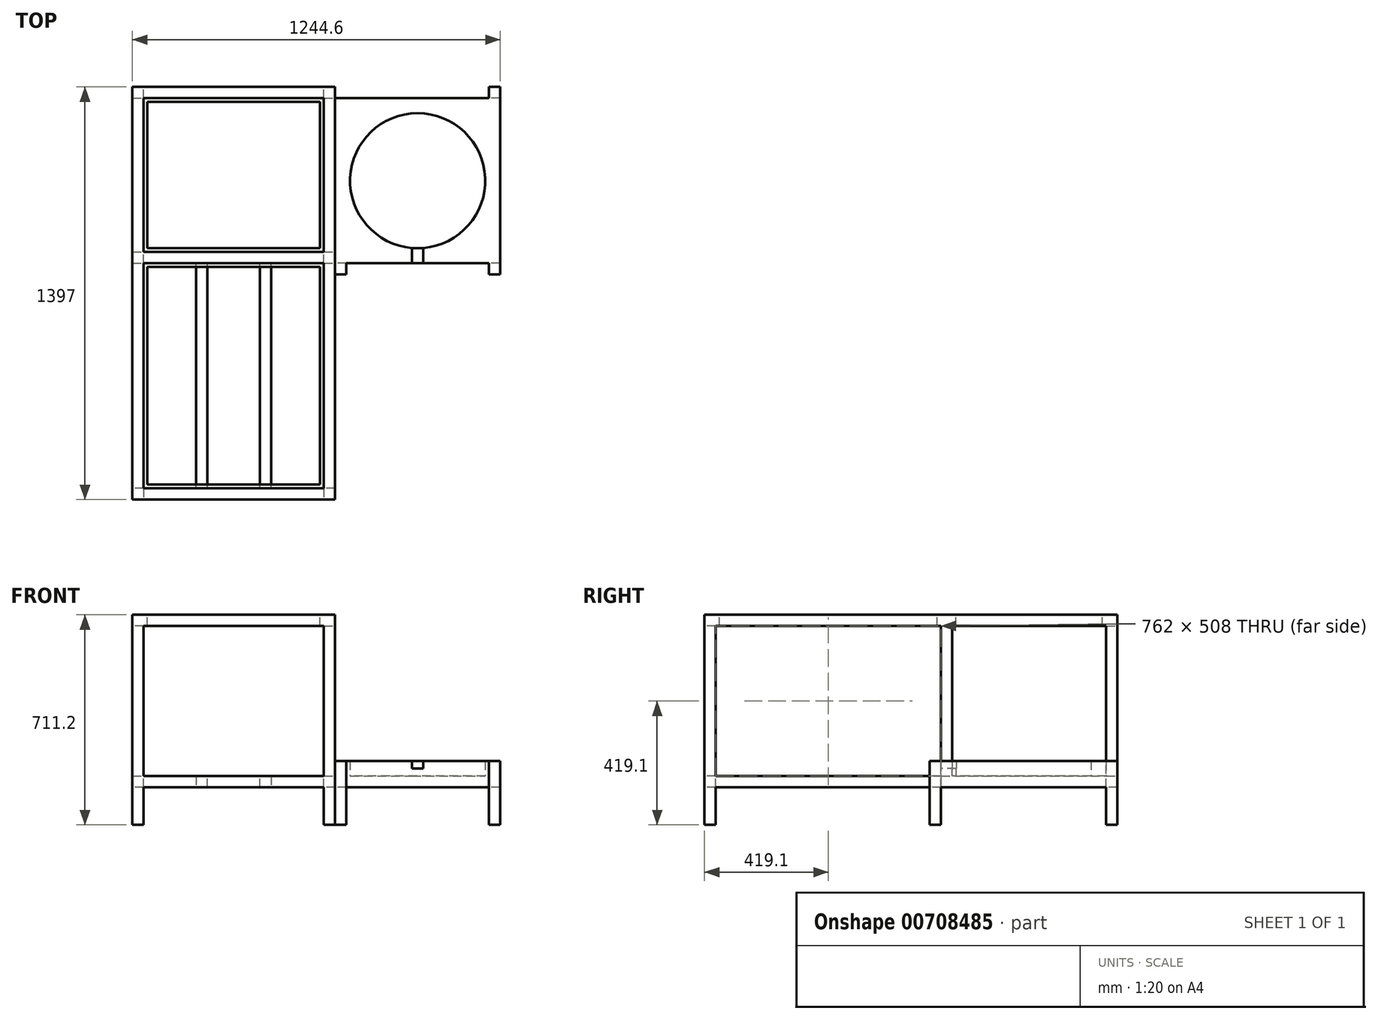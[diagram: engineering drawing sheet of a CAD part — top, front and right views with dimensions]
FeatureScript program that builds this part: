
annotation { "Feature Type Name" : "Feature", "Feature Type Description" : "" }
export const myFeature = defineFeature(function(context is Context, id is Id, definition is map)
    precondition{}
    {
        {
            var Q0;
            Q0=qCreatedBy(makeId("Top.planeOp"),FACE);
            var sketch = newSketch(context, id + "F0", { "sketchPlane" : qUnion([Q0])});
            skLineSegment(sketch, "E0.bottom", {"start": v(-342.9, -698.5) * mm, "end": v(342.9, -698.5) * mm});
            skLineSegment(sketch, "E0.top", {"start": v(-342.9, 698.5) * mm, "end": v(342.9, 698.5) * mm});
            skLineSegment(sketch, "E0.left", {"start": v(-342.9, -698.5) * mm, "end": v(-342.9, 698.5) * mm});
            skLineSegment(sketch, "E0.right", {"start": v(342.9, -698.5) * mm, "end": v(342.9, 698.5) * mm});
            skPoint(sketch, "E0.middle", {"position": v(0, 0) * mm});
            skSolve(sketch);
        }
        {
            var Q0;
            Q0 = qSketchRegion(id + "F0", true);
            extrude(context, id + "F1", {"entities" : qUnion([Q0]), "depth" : 711.2 * mm, "offsetDistance" : 25.4 * mm});
        }
        {
            var Q0;
            Q0=makeQuery(id+"F1.opExtrude","SWEPT_FACE",FACE,{"disambiguationData":[OSD([sQuery(id+"F0.wireOp",EDGE,"E0.bottom")])]});
            var sketch = newSketch(context, id + "F2", { "sketchPlane" : qUnion([Q0])});
            skLineSegment(sketch, "E1.0", {"start": v(-304.8, 673.1) * mm, "end": v(-304.8, 165.1) * mm});
            skLineSegment(sketch, "E1.1", {"start": v(-304.8, 673.1) * mm, "end": v(304.8, 673.1) * mm});
            skLineSegment(sketch, "E1.2", {"start": v(304.8, 673.1) * mm, "end": v(304.8, 165.1) * mm});
            skLineSegment(sketch, "E1.3", {"start": v(-304.8, 38.1) * mm, "end": v(304.8, 38.1) * mm});
            skLineSegment(sketch, "E2.0", {"start": v(-304.8, 165.1) * mm, "end": v(304.8, 165.1) * mm});
            skLineSegment(sketch, "E3.0", {"start": v(-304.8, 127) * mm, "end": v(304.8, 127) * mm});
            skLineSegment(sketch, "E4.trimOffspring", {"start": v(-304.8, 127) * mm, "end": v(-304.8, 38.1) * mm});
            skLineSegment(sketch, "E5.trimOffspring", {"start": v(304.8, 127) * mm, "end": v(304.8, 38.1) * mm});
            skSolve(sketch);
        }
        {
            var Q0;
            Q0 = qSketchRegion(id + "F2", true);
            extrude(context, id + "F3", {"entities" : qUnion([Q0]), "operationType" : NewBodyOperationType.REMOVE, "oppositeDirection" : true, "depth" : 800.1 * mm, "offsetDistance" : 25.4 * mm});
        }
        {
            var Q0;
            Q0=makeQuery(id+"F3.boolean.opBoolean","COPY",FACE,{"derivedFrom":makeQuery(id+"F3.opExtrude","CAP_FACE",FACE,{"disambiguationData":[OSD([sQuery(id+"F2.wireOp",EDGE,"E1.3"),sQuery(id+"F2.wireOp",EDGE,"E3.0"),sQuery(id+"F2.wireOp",EDGE,"E4.trimOffspring"),sQuery(id+"F2.wireOp",EDGE,"E5.trimOffspring")])],"isStart":false})});
            var sketch = newSketch(context, id + "F4", { "sketchPlane" : qUnion([Q0])});
            skLineSegment(sketch, "E6.0", {"start": v(-304.8, 127) * mm, "end": v(304.8, 127) * mm});
            skLineSegment(sketch, "E6.1", {"start": v(-304.8, 127) * mm, "end": v(-304.8, 38.1) * mm});
            skLineSegment(sketch, "E6.2", {"start": v(-304.8, 38.1) * mm, "end": v(304.8, 38.1) * mm});
            skLineSegment(sketch, "E6.3", {"start": v(304.8, 127) * mm, "end": v(304.8, 38.1) * mm});
            skSolve(sketch);
        }
        {
            var Q0;
            Q0 = qSketchRegion(id + "F4", true);
            extrude(context, id + "F5", {"entities" : qUnion([Q0]), "operationType" : NewBodyOperationType.REMOVE, "endBound" : BoundingType.THROUGH_ALL, "oppositeDirection" : true, "depth" : 25.4 * mm, "offsetDistance" : 25.4 * mm});
        }
        {
            var Q0;
            Q0=makeQuery(id+"F1.opExtrude","CAP_FACE",FACE,{"disambiguationData":[OSD([sQuery(id+"F0.wireOp",EDGE,"E0.bottom"),sQuery(id+"F0.wireOp",EDGE,"E0.top"),sQuery(id+"F0.wireOp",EDGE,"E0.left"),sQuery(id+"F0.wireOp",EDGE,"E0.right")])],"isStart":false});
            var sketch = newSketch(context, id + "F6", { "sketchPlane" : qUnion([Q0])});
            skLineSegment(sketch, "E7.0", {"start": v(-304.8, 101.6) * mm, "end": v(-304.8, -660.4) * mm});
            skLineSegment(sketch, "E8.0", {"start": v(-304.8, 101.6) * mm, "end": v(304.8, 101.6) * mm});
            skLineSegment(sketch, "E9.0", {"start": v(304.8, 101.6) * mm, "end": v(304.8, -660.4) * mm});
            skLineSegment(sketch, "E10.0", {"start": v(-304.8, -660.4) * mm, "end": v(304.8, -660.4) * mm});
            skPoint(sketch, "E11.0.start.orphan", {"position": v(-304.8, -698.5) * mm});
            skPoint(sketch, "E12.orphan", {"position": v(304.8, -698.5) * mm});
            skSolve(sketch);
        }
        {
            var Q0;
            Q0 = qSketchRegion(id + "F6", true);
            extrude(context, id + "F7", {"entities" : qUnion([Q0]), "operationType" : NewBodyOperationType.REMOVE, "oppositeDirection" : true, "depth" : 3 / 203.2 * mm, "offsetDistance" : 25.4 * mm});
        }
        {
            var Q0;
            Q0=makeQuery(id+"F7.boolean.opBoolean","COPY",FACE,{"derivedFrom":makeQuery(id+"F7.opExtrude","CAP_FACE",FACE,{"disambiguationData":[OSD([sQuery(id+"F6.wireOp",EDGE,"E7.0"),sQuery(id+"F6.wireOp",EDGE,"E8.0"),sQuery(id+"F6.wireOp",EDGE,"E9.0"),sQuery(id+"F6.wireOp",EDGE,"E10.0")])],"isStart":false})});
            var sketch = newSketch(context, id + "F8", { "sketchPlane" : qUnion([Q0])});
            skLineSegment(sketch, "E13.0", {"start": v(-304.8, 101.6) * mm, "end": v(-304.8, -660.4) * mm});
            skLineSegment(sketch, "E14.0", {"start": v(-304.8, 101.6) * mm, "end": v(304.8, 101.6) * mm});
            skLineSegment(sketch, "E15.0", {"start": v(304.8, 101.6) * mm, "end": v(304.8, -660.4) * mm});
            skLineSegment(sketch, "E16.0", {"start": v(-304.8, -660.4) * mm, "end": v(304.8, -660.4) * mm});
            skLineSegment(sketch, "E17.0", {"start": v(-292.1, 88.9) * mm, "end": v(292.1, 88.9) * mm});
            skLineSegment(sketch, "E17.1", {"start": v(-292.1, 88.9) * mm, "end": v(-292.1, -647.7) * mm});
            skLineSegment(sketch, "E17.2", {"start": v(-292.1, -647.7) * mm, "end": v(292.1, -647.7) * mm});
            skLineSegment(sketch, "E17.3", {"start": v(292.1, 88.9) * mm, "end": v(292.1, -647.7) * mm});
            skSolve(sketch);
        }
        {
            var Q0;
            Q0=makeQuery(id+"F8.imprint","IMPRINT",FACE,{"disambiguationData":[TD([[makeQuery(id+"F8.imprint","IMPRINT",EDGE,{"derivedFrom":sQuery(id+"F8.wireOp",EDGE,"E17.0")}),-1.0]])]});
            extrude(context, id + "F9", {"entities" : qUnion([Q0]), "operationType" : NewBodyOperationType.REMOVE, "oppositeDirection" : true, "depth" : 50.8 * mm, "offsetDistance" : 25.4 * mm});
        }
        {
            var Q0;
            Q0=makeQuery(id+"F1.opExtrude","SWEPT_FACE",FACE,{"disambiguationData":[OSD([sQuery(id+"F0.wireOp",EDGE,"E0.bottom")])]});
            var sketch = newSketch(context, id + "F10", { "sketchPlane" : qUnion([Q0])});
            skLineSegment(sketch, "E18", {"start": v(-304.8, 38.1) * mm, "end": v(-304.8, 0) * mm});
            skLineSegment(sketch, "E19", {"start": v(-304.8, 0) * mm, "end": v(304.8, 0) * mm});
            skLineSegment(sketch, "E20", {"start": v(304.8, 0) * mm, "end": v(304.8, 38.1) * mm});
            skLineSegment(sketch, "E21", {"start": v(304.8, 38.1) * mm, "end": v(-304.8, 38.1) * mm});
            skSolve(sketch);
        }
        {
            var Q0;
            Q0 = qSketchRegion(id + "F10", true);
            extrude(context, id + "F11", {"entities" : qUnion([Q0]), "operationType" : NewBodyOperationType.REMOVE, "endBound" : BoundingType.THROUGH_ALL, "oppositeDirection" : true, "depth" : 25.4 * mm, "offsetDistance" : 25.4 * mm});
        }
        {
            var Q0;
            Q0=makeQuery(id+"F1.opExtrude","SWEPT_FACE",FACE,{"disambiguationData":[OSD([sQuery(id+"F0.wireOp",EDGE,"E0.left")])]});
            var sketch = newSketch(context, id + "F12", { "sketchPlane" : qUnion([Q0])});
            skLineSegment(sketch, "E22.0", {"start": v(-101.6, 673.1) * mm, "end": v(-101.6, 165.1) * mm});
            skLineSegment(sketch, "E23.0", {"start": v(-660.4, 127) * mm, "end": v(660.4, 127) * mm});
            skLineSegment(sketch, "E24.0", {"start": v(-101.6, 165.1) * mm, "end": v(660.4, 165.1) * mm});
            skLineSegment(sketch, "E25.0", {"start": v(-660.4, 0) * mm, "end": v(-660.4, 127) * mm});
            skLineSegment(sketch, "E26.0", {"start": v(660.4, 673.1) * mm, "end": v(660.4, 165.1) * mm});
            skLineSegment(sketch, "E27.0", {"start": v(-101.6, 673.1) * mm, "end": v(660.4, 673.1) * mm});
            skLineSegment(sketch, "E28.trimOffspring", {"start": v(660.4, 127) * mm, "end": v(660.4, 0) * mm});
            skLineSegment(sketch, "E29", {"start": v(660.4, 0) * mm, "end": v(-660.4, 0) * mm});
            skSolve(sketch);
        }
        {
            var Q0;
            Q0 = qSketchRegion(id + "F12", true);
            extrude(context, id + "F13", {"entities" : qUnion([Q0]), "operationType" : NewBodyOperationType.REMOVE, "endBound" : BoundingType.THROUGH_ALL, "oppositeDirection" : true, "depth" : 25.4 * mm, "offsetDistance" : 25.4 * mm});
        }
        {
            var Q0;
            Q0=makeQuery(id+"F1.opExtrude","SWEPT_FACE",FACE,{"disambiguationData":[OSD([sQuery(id+"F0.wireOp",EDGE,"E0.top")])]});
            var sketch = newSketch(context, id + "F14", { "sketchPlane" : qUnion([Q0])});
            skLineSegment(sketch, "E30.0", {"start": v(304.8, 165.1) * mm, "end": v(-304.8, 165.1) * mm});
            skLineSegment(sketch, "E31.0", {"start": v(304.8, 673.1) * mm, "end": v(-304.8, 673.1) * mm});
            skLineSegment(sketch, "E32.0", {"start": v(304.8, 673.1) * mm, "end": v(304.8, 165.1) * mm});
            skLineSegment(sketch, "E33.0", {"start": v(-304.8, 673.1) * mm, "end": v(-304.8, 165.1) * mm});
            skSolve(sketch);
        }
        {
            var Q0;
            Q0 = qSketchRegion(id + "F14", true);
            extrude(context, id + "F15", {"entities" : qUnion([Q0]), "operationType" : NewBodyOperationType.REMOVE, "oppositeDirection" : true, "depth" : 584.2 * mm, "offsetDistance" : 25.4 * mm});
        }
        {
            var Q0;
            Q0=makeQuery(id+"F1.opExtrude","CAP_FACE",FACE,{"disambiguationData":[OSD([sQuery(id+"F0.wireOp",EDGE,"E0.bottom"),sQuery(id+"F0.wireOp",EDGE,"E0.top"),sQuery(id+"F0.wireOp",EDGE,"E0.left"),sQuery(id+"F0.wireOp",EDGE,"E0.right")])],"isStart":false});
            var sketch = newSketch(context, id + "F16", { "sketchPlane" : qUnion([Q0])});
            skLineSegment(sketch, "E34.0", {"start": v(-304.8, 139.7) * mm, "end": v(304.8, 139.7) * mm});
            skLineSegment(sketch, "E35.0", {"start": v(-304.8, 660.4) * mm, "end": v(304.8, 660.4) * mm});
            skLineSegment(sketch, "E36", {"start": v(-304.8, 139.7) * mm, "end": v(-304.8, 660.4) * mm});
            skLineSegment(sketch, "E37", {"start": v(304.8, 139.7) * mm, "end": v(304.8, 660.4) * mm});
            skSolve(sketch);
        }
        {
            var Q0;
            Q0 = qSketchRegion(id + "F16", true);
            extrude(context, id + "F17", {"entities" : qUnion([Q0]), "operationType" : NewBodyOperationType.REMOVE, "oppositeDirection" : true, "depth" : 3 / 203.2 * mm, "offsetDistance" : 25.4 * mm});
        }
        {
            var Q0;
            Q0=makeQuery(id+"F17.boolean.opBoolean","COPY",FACE,{"derivedFrom":makeQuery(id+"F17.opExtrude","CAP_FACE",FACE,{"disambiguationData":[OSD([sQuery(id+"F16.wireOp",EDGE,"E34.0"),sQuery(id+"F16.wireOp",EDGE,"E35.0"),sQuery(id+"F16.wireOp",EDGE,"E36"),sQuery(id+"F16.wireOp",EDGE,"E37")])],"isStart":false})});
            var sketch = newSketch(context, id + "F18", { "sketchPlane" : qUnion([Q0])});
            skLineSegment(sketch, "E38.0", {"start": v(-292.1, 152.4) * mm, "end": v(-292.1, 647.7) * mm});
            skLineSegment(sketch, "E38.1", {"start": v(-292.1, 152.4) * mm, "end": v(292.1, 152.4) * mm});
            skLineSegment(sketch, "E38.2", {"start": v(292.1, 152.4) * mm, "end": v(292.1, 647.7) * mm});
            skLineSegment(sketch, "E38.3", {"start": v(-292.1, 647.7) * mm, "end": v(292.1, 647.7) * mm});
            skSolve(sketch);
        }
        {
            var Q0;
            Q0 = qSketchRegion(id + "F18", true);
            var Q1;
            Q1=makeQuery(id+"F15.boolean.opBoolean","COPY",FACE,{"derivedFrom":makeQuery(id+"F15.opExtrude","SWEPT_FACE",FACE,{"disambiguationData":[OSD([sQuery(id+"F14.wireOp",EDGE,"E31.0")])]})});
            extrude(context, id + "F19", {"entities" : qUnion([Q0]), "operationType" : NewBodyOperationType.REMOVE, "endBound" : BoundingType.UP_TO_SURFACE, "oppositeDirection" : true, "depth" : 25.4 * mm, "endBoundEntityFace" : qUnion([Q1]), "offsetDistance" : 25.4 * mm});
        }
        {
            var Q0;
            Q0=makeQuery(id+"F1.opExtrude","SWEPT_FACE",FACE,{"disambiguationData":[OSD([sQuery(id+"F0.wireOp",EDGE,"E0.right")])]});
            var sketch = newSketch(context, id + "F20", { "sketchPlane" : qUnion([Q0])});
            skLineSegment(sketch, "E39.0", {"start": v(647.7, 673.1) * mm, "end": v(152.4, 673.1) * mm});
            skLineSegment(sketch, "E40.0", {"start": v(139.7, 165.1) * mm, "end": v(660.4, 165.1) * mm});
            skLineSegment(sketch, "E41", {"start": v(152.4, 673.1) * mm, "end": v(139.7, 673.1) * mm});
            skLineSegment(sketch, "E42", {"start": v(139.7, 673.1) * mm, "end": v(139.7, 165.1) * mm});
            skLineSegment(sketch, "E43", {"start": v(647.7, 673.1) * mm, "end": v(660.4, 673.1) * mm});
            skLineSegment(sketch, "E44", {"start": v(660.4, 673.1) * mm, "end": v(660.4, 165.1) * mm});
            skPoint(sketch, "E45.orphan", {"position": v(698.5, 165.1) * mm});
            skPoint(sketch, "E46.orphan", {"position": v(114.3, 165.1) * mm});
            skSolve(sketch);
        }
        {
            var Q0;
            Q0 = qSketchRegion(id + "F20", true);
            extrude(context, id + "F21", {"entities" : qUnion([Q0]), "operationType" : NewBodyOperationType.REMOVE, "endBound" : BoundingType.THROUGH_ALL, "oppositeDirection" : true, "depth" : 25.4 * mm, "offsetDistance" : 25.4 * mm});
        }
        {
            var Q0;
            Q0=makeQuery(id+"F1.opExtrude","SWEPT_FACE",FACE,{"disambiguationData":[OSD([sQuery(id+"F0.wireOp",EDGE,"E0.right")])]});
            var sketch = newSketch(context, id + "F22", { "sketchPlane" : qUnion([Q0])});
            skLineSegment(sketch, "E47", {"start": v(660.4, 165.1) * mm, "end": v(101.6, 165.1) * mm});
            skLineSegment(sketch, "E48", {"start": v(101.6, 165.1) * mm, "end": v(101.6, 127) * mm});
            skLineSegment(sketch, "E49", {"start": v(101.6, 127) * mm, "end": v(660.4, 127) * mm});
            skLineSegment(sketch, "E50", {"start": v(660.4, 127) * mm, "end": v(660.4, 165.1) * mm});
            skSolve(sketch);
        }
        {
            var Q0;
            Q0 = qSketchRegion(id + "F22", true);
            extrude(context, id + "F23", {"entities" : qUnion([Q0]), "operationType" : NewBodyOperationType.ADD, "depth" : 558.8 * mm, "offsetDistance" : 25.4 * mm});
        }
        {
            var Q0;
            Q0=makeQuery(id+"F23.boolean.opBoolean","MERGE",FACE,{"derivedFrom":[makeQuery(id+"F21.boolean.opBoolean","MERGE",FACE,{"derivedFrom":[makeQuery(id+"F15.boolean.opBoolean","COPY",FACE,{"derivedFrom":makeQuery(id+"F15.opExtrude","SWEPT_FACE",FACE,{"disambiguationData":[OSD([sQuery(id+"F14.wireOp",EDGE,"E30.0")])]})}),makeQuery(id+"F21.opExtrude","SWEPT_FACE",FACE,{"disambiguationData":[OSD([sQuery(id+"F20.wireOp",EDGE,"E40.0")])]})]}),makeQuery(id+"F23.opExtrude","SWEPT_FACE",FACE,{"disambiguationData":[OSD([sQuery(id+"F22.wireOp",EDGE,"E47")])]})]});
            var sketch = newSketch(context, id + "F24", { "sketchPlane" : qUnion([Q0])});
            skPoint(sketch, "E51", {"position": v(622.3, 381) * mm});
            skCircle(sketch, "E52", {"center": v(622.3, 381) * mm, "radius": 228.6 * mm});
            skPoint(sketch, "E53.orphan", {"position": v(342.9, -698.5) * mm});
            skPoint(sketch, "E54.orphan", {"position": v(342.9, 698.5) * mm});
            skLineSegment(sketch, "E55", {"start": v(901.7, 660.4) * mm, "end": v(901.7, 101.6) * mm});
            skLineSegment(sketch, "E56", {"start": v(901.7, 101.6) * mm, "end": v(342.93, 101.6) * mm});
            skLineSegment(sketch, "E57", {"start": v(342.93, 101.6) * mm, "end": v(342.93, 660.4) * mm});
            skLineSegment(sketch, "E58", {"start": v(342.93, 660.4) * mm, "end": v(901.7, 660.4) * mm});
            skSolve(sketch);
        }
        {
            var Q0;
            Q0 = qSketchRegion(id + "F24", true);
            extrude(context, id + "F25", {"entities" : qUnion([Q0]), "operationType" : NewBodyOperationType.ADD, "depth" : 50.8 * mm, "offsetDistance" : 25.4 * mm});
        }
        {
            var Q0;
            Q0=makeQuery(id+"F25.boolean.opBoolean","MERGE",FACE,{"derivedFrom":[makeQuery(id+"F23.opExtrude","SWEPT_FACE",FACE,{"disambiguationData":[OSD([sQuery(id+"F22.wireOp",EDGE,"E48")])]}),makeQuery(id+"F25.opExtrude","SWEPT_FACE",FACE,{"disambiguationData":[OSD([sQuery(id+"F24.wireOp",EDGE,"E56")])]})]});
            var sketch = newSketch(context, id + "F26", { "sketchPlane" : qUnion([Q0])});
            skLineSegment(sketch, "E59.bottom", {"start": v(603.25, 190.5) * mm, "end": v(641.35, 190.5) * mm});
            skLineSegment(sketch, "E59.right", {"start": v(641.35, 190.5) * mm, "end": v(641.35, 215.9) * mm});
            skPoint(sketch, "E59.middle", {"position": v(622.3, 215.9) * mm});
            skPoint(sketch, "E59.top.end.orphan", {"position": v(641.35, 241.3) * mm});
            skPoint(sketch, "E59.left.end.orphan", {"position": v(603.25, 241.3) * mm});
            skLineSegment(sketch, "E60", {"start": v(603.25, 190.5) * mm, "end": v(603.25, 215.9) * mm});
            skLineSegment(sketch, "E61", {"start": v(641.35, 215.9) * mm, "end": v(603.25, 215.9) * mm});
            skSolve(sketch);
        }
        {
            var Q0;
            Q0 = qSketchRegion(id + "F26", true);
            var Q1;
            Q1=makeQuery(id+"F25.opExtrude","SWEPT_FACE",FACE,{"disambiguationData":[OSD([sQuery(id+"F24.wireOp",EDGE,"E52")])]});
            extrude(context, id + "F27", {"entities" : qUnion([Q0]), "operationType" : NewBodyOperationType.REMOVE, "endBound" : BoundingType.UP_TO_SURFACE, "oppositeDirection" : true, "depth" : 25.4 * mm, "endBoundEntityFace" : qUnion([Q1]), "offsetDistance" : 25.4 * mm});
        }
        {
            var Q0;
            Q0=makeQuery(id+"F23.boolean.opBoolean","MERGE",FACE,{"derivedFrom":[makeQuery(id+"F13.boolean.opBoolean","MERGE",FACE,{"derivedFrom":[makeQuery(id+"F5.boolean.opBoolean","MERGE",FACE,{"derivedFrom":[makeQuery(id+"F3.boolean.opBoolean","COPY",FACE,{"derivedFrom":makeQuery(id+"F3.opExtrude","SWEPT_FACE",FACE,{"disambiguationData":[OSD([sQuery(id+"F2.wireOp",EDGE,"E3.0")])]})}),makeQuery(id+"F5.opExtrude","SWEPT_FACE",FACE,{"disambiguationData":[OSD([sQuery(id+"F4.wireOp",EDGE,"E6.0")])]})]}),makeQuery(id+"F13.opExtrude","SWEPT_FACE",FACE,{"disambiguationData":[OSD([sQuery(id+"F12.wireOp",EDGE,"E23.0")])]})]}),makeQuery(id+"F23.opExtrude","SWEPT_FACE",FACE,{"disambiguationData":[OSD([sQuery(id+"F22.wireOp",EDGE,"E49")])]})]});
            var sketch = newSketch(context, id + "F28", { "sketchPlane" : qUnion([Q0])});
            skLineSegment(sketch, "E62.bottom", {"start": v(901.7, -101.6) * mm, "end": v(863.6, -101.6) * mm});
            skLineSegment(sketch, "E62.top", {"start": v(901.7, -63.5) * mm, "end": v(863.6, -63.5) * mm});
            skLineSegment(sketch, "E62.left", {"start": v(901.7, -101.6) * mm, "end": v(901.7, -63.5) * mm});
            skLineSegment(sketch, "E62.right", {"start": v(863.6, -101.6) * mm, "end": v(863.6, -63.5) * mm});
            skLineSegment(sketch, "E63.bottom", {"start": v(901.7, -660.4) * mm, "end": v(863.6, -660.4) * mm});
            skLineSegment(sketch, "E63.top", {"start": v(901.7, -698.5) * mm, "end": v(863.6, -698.5) * mm});
            skLineSegment(sketch, "E63.left", {"start": v(901.7, -660.4) * mm, "end": v(901.7, -698.5) * mm});
            skLineSegment(sketch, "E63.right", {"start": v(863.6, -660.4) * mm, "end": v(863.6, -698.5) * mm});
            skLineSegment(sketch, "E64.bottom", {"start": v(342.91, -101.6) * mm, "end": v(381.01, -101.6) * mm});
            skLineSegment(sketch, "E64.top", {"start": v(342.91, -63.5) * mm, "end": v(381.01, -63.5) * mm});
            skLineSegment(sketch, "E64.left", {"start": v(342.91, -101.6) * mm, "end": v(342.91, -63.5) * mm});
            skLineSegment(sketch, "E64.right", {"start": v(381.01, -101.6) * mm, "end": v(381.01, -63.5) * mm});
            skSolve(sketch);
        }
        {
            var Q0;
            Q0 = qSketchRegion(id + "F28", true);
            var Q1;
            {var subQ2=sQuery(id+"F0.wireOp",EDGE,"E0.left");var subQ3=makeQuery(id+"F1.opExtrude","SWEPT_FACE",FACE,{"disambiguationData":[OSD([subQ2])]});var subQ4=sQuery(id+"F0.wireOp",EDGE,"E0.top");var subQ5=makeQuery(id+"F1.opExtrude","SWEPT_FACE",FACE,{"disambiguationData":[OSD([subQ4])]});var subQ7=sQuery(id+"F0.wireOp",EDGE,"E0.bottom");Q1=makeQuery(id+"F13.boolean.opBoolean","SPLIT",FACE,{"disambiguationData":[TD([subQ5])],"derivedFrom":makeQuery(id+"F11.boolean.opBoolean","SPLIT",FACE,{"disambiguationData":[TD([subQ3])],"derivedFrom":makeQuery(id+"F1.opExtrude","CAP_FACE",FACE,{"disambiguationData":[OSD([subQ7,subQ4,subQ2,sQuery(id+"F0.wireOp",EDGE,"E0.right")])],"isStart":true})})});}
            var Q2;
            Q2=makeQuery(id+"F25.opExtrude","CAP_FACE",FACE,{"disambiguationData":[OSD([sQuery(id+"F24.wireOp",EDGE,"E52"),sQuery(id+"F24.wireOp",EDGE,"E55"),sQuery(id+"F24.wireOp",EDGE,"E56"),sQuery(id+"F24.wireOp",EDGE,"E57"),sQuery(id+"F24.wireOp",EDGE,"E58")])],"isStart":false});
            extrude(context, id + "F29", {"entities" : qUnion([Q0]), "operationType" : NewBodyOperationType.ADD, "endBound" : BoundingType.UP_TO_SURFACE, "depth" : 25.4 * mm, "endBoundEntityFace" : qUnion([Q1]), "offsetDistance" : 25.4 * mm, "hasSecondDirection" : true, "secondDirectionBound" : SecondDirectionBoundingType.UP_TO_SURFACE, "secondDirectionOppositeDirection" : true, "secondDirectionDepth" : 25.4 * mm, "secondDirectionBoundEntityFace" : qUnion([Q2])});
        }
        {
            var Q0;
            Q0=makeQuery(id+"F15.boolean.opBoolean","COPY",FACE,{"derivedFrom":makeQuery(id+"F15.opExtrude","CAP_FACE",FACE,{"disambiguationData":[OSD([sQuery(id+"F14.wireOp",EDGE,"E30.0"),sQuery(id+"F14.wireOp",EDGE,"E31.0"),sQuery(id+"F14.wireOp",EDGE,"E32.0"),sQuery(id+"F14.wireOp",EDGE,"E33.0")])],"isStart":false})});
            var sketch = newSketch(context, id + "F30", { "sketchPlane" : qUnion([Q0])});
            skLineSegment(sketch, "E65.0", {"start": v(304.8, 673.1) * mm, "end": v(304.8, 165.1) * mm});
            skLineSegment(sketch, "E66.0", {"start": v(304.8, 673.1) * mm, "end": v(-304.8, 673.1) * mm});
            skLineSegment(sketch, "E67.0", {"start": v(-304.8, 673.1) * mm, "end": v(-304.8, 165.1) * mm});
            skLineSegment(sketch, "E68.0", {"start": v(304.8, 165.1) * mm, "end": v(-304.8, 165.1) * mm});
            skSolve(sketch);
        }
        {
            var Q0;
            Q0 = qSketchRegion(id + "F30", true);
            var Q1;
            Q1=makeQuery(id+"F13.boolean.opBoolean","MERGE",FACE,{"derivedFrom":[makeQuery(id+"F3.boolean.opBoolean","COPY",FACE,{"derivedFrom":makeQuery(id+"F3.opExtrude","CAP_FACE",FACE,{"disambiguationData":[OSD([sQuery(id+"F2.wireOp",EDGE,"E1.0"),sQuery(id+"F2.wireOp",EDGE,"E1.1"),sQuery(id+"F2.wireOp",EDGE,"E1.2"),sQuery(id+"F2.wireOp",EDGE,"E2.0")])],"isStart":false})}),makeQuery(id+"F13.opExtrude","SWEPT_FACE",FACE,{"disambiguationData":[OSD([sQuery(id+"F12.wireOp",EDGE,"E22.0")])]})]});
            extrude(context, id + "F31", {"entities" : qUnion([Q0]), "operationType" : NewBodyOperationType.REMOVE, "endBound" : BoundingType.UP_TO_SURFACE, "oppositeDirection" : true, "depth" : 25.4 * mm, "endBoundEntityFace" : qUnion([Q1]), "offsetDistance" : 25.4 * mm});
        }
        {
            var Q0;
            {var subQ0=makeQuery(id+"F13.opExtrude","SWEPT_FACE",FACE,{"disambiguationData":[OSD([sQuery(id+"F12.wireOp",EDGE,"E24.0")])]});var subQ1=sQuery(id+"F2.wireOp",EDGE,"E2.0");var subQ2=makeQuery(id+"F3.boolean.opBoolean","COPY",FACE,{"derivedFrom":makeQuery(id+"F3.opExtrude","SWEPT_FACE",FACE,{"disambiguationData":[OSD([subQ1])]})});var subQ6=sQuery(id+"F14.wireOp",EDGE,"E30.0");var subQ8=makeQuery(id+"F15.boolean.opBoolean","COPY",FACE,{"derivedFrom":makeQuery(id+"F15.opExtrude","SWEPT_FACE",FACE,{"disambiguationData":[OSD([subQ6])]})});var subQ12=makeQuery(id+"F21.opExtrude","SWEPT_FACE",FACE,{"disambiguationData":[OSD([sQuery(id+"F20.wireOp",EDGE,"E40.0")])]});Q0=makeQuery(id+"F31.boolean.opBoolean","MERGE",FACE,{"derivedFrom":[makeQuery(id+"F13.boolean.opBoolean","MERGE",FACE,{"derivedFrom":[subQ2,subQ0]}),makeQuery(id+"F25.boolean.opBoolean","SPLIT",FACE,{"disambiguationData":[TD([makeQuery(id+"F1.opExtrude","SWEPT_FACE",FACE,{"disambiguationData":[OSD([sQuery(id+"F0.wireOp",EDGE,"E0.top")])]})])],"derivedFrom":makeQuery(id+"F23.boolean.opBoolean","MERGE",FACE,{"derivedFrom":[makeQuery(id+"F21.boolean.opBoolean","MERGE",FACE,{"derivedFrom":[subQ8,subQ12]}),makeQuery(id+"F23.opExtrude","SWEPT_FACE",FACE,{"disambiguationData":[OSD([sQuery(id+"F22.wireOp",EDGE,"E47")])]})]})}),makeQuery(id+"F31.opExtrude","SWEPT_FACE",FACE,{"disambiguationData":[OSD([sQuery(id+"F30.wireOp",EDGE,"E68.0")])]})]});}
            var sketch = newSketch(context, id + "F32", { "sketchPlane" : qUnion([Q0])});
            skLineSegment(sketch, "E69", {"start": v(-304.8, 101.6) * mm, "end": v(304.8, 101.6) * mm});
            skLineSegment(sketch, "E70", {"start": v(304.8, 101.6) * mm, "end": v(304.8, -660.4) * mm});
            skLineSegment(sketch, "E71", {"start": v(-304.8, -660.4) * mm, "end": v(304.8, -660.4) * mm});
            skLineSegment(sketch, "E72", {"start": v(-304.8, -660.4) * mm, "end": v(-304.8, 101.6) * mm});
            skSolve(sketch);
        }
        {
            var Q0;
            Q0 = qSketchRegion(id + "F32", true);
            extrude(context, id + "F33", {"entities" : qUnion([Q0]), "operationType" : NewBodyOperationType.REMOVE, "endBound" : BoundingType.THROUGH_ALL, "oppositeDirection" : true, "depth" : 25.4 * mm, "offsetDistance" : 25.4 * mm});
        }
        {
            var Q0;
            Q0=makeQuery(id+"F33.boolean.opBoolean","COPY",FACE,{"derivedFrom":makeQuery(id+"F33.opExtrude","SWEPT_FACE",FACE,{"disambiguationData":[OSD([sQuery(id+"F32.wireOp",EDGE,"E69")])]})});
            var sketch = newSketch(context, id + "F34", { "sketchPlane" : qUnion([Q0])});
            skLineSegment(sketch, "E73.0", {"start": v(88.9, 127) * mm, "end": v(88.9, 165.1) * mm});
            skLineSegment(sketch, "E74", {"start": v(88.9, 165.1) * mm, "end": v(127, 165.1) * mm});
            skLineSegment(sketch, "E75", {"start": v(127, 165.1) * mm, "end": v(127, 127) * mm});
            skLineSegment(sketch, "E76", {"start": v(127, 127) * mm, "end": v(88.9, 127) * mm});
            skLineSegment(sketch, "E77.MirrorCS", {"start": v(-88.9, 127) * mm, "end": v(-88.9, 165.1) * mm});
            skLineSegment(sketch, "E78.MirrorCS", {"start": v(-127, 127) * mm, "end": v(-88.9, 127) * mm});
            skLineSegment(sketch, "E79.MirrorCS", {"start": v(-127, 165.1) * mm, "end": v(-127, 127) * mm});
            skLineSegment(sketch, "E80.MirrorCS", {"start": v(-88.9, 165.1) * mm, "end": v(-127, 165.1) * mm});
            skSolve(sketch);
        }
        {
            var Q0;
            Q0 = qSketchRegion(id + "F34", true);
            extrude(context, id + "F35", {"entities" : qUnion([Q0]), "operationType" : NewBodyOperationType.ADD, "endBound" : BoundingType.UP_TO_NEXT, "depth" : 25.4 * mm, "offsetDistance" : 25.4 * mm});
        }
    });
